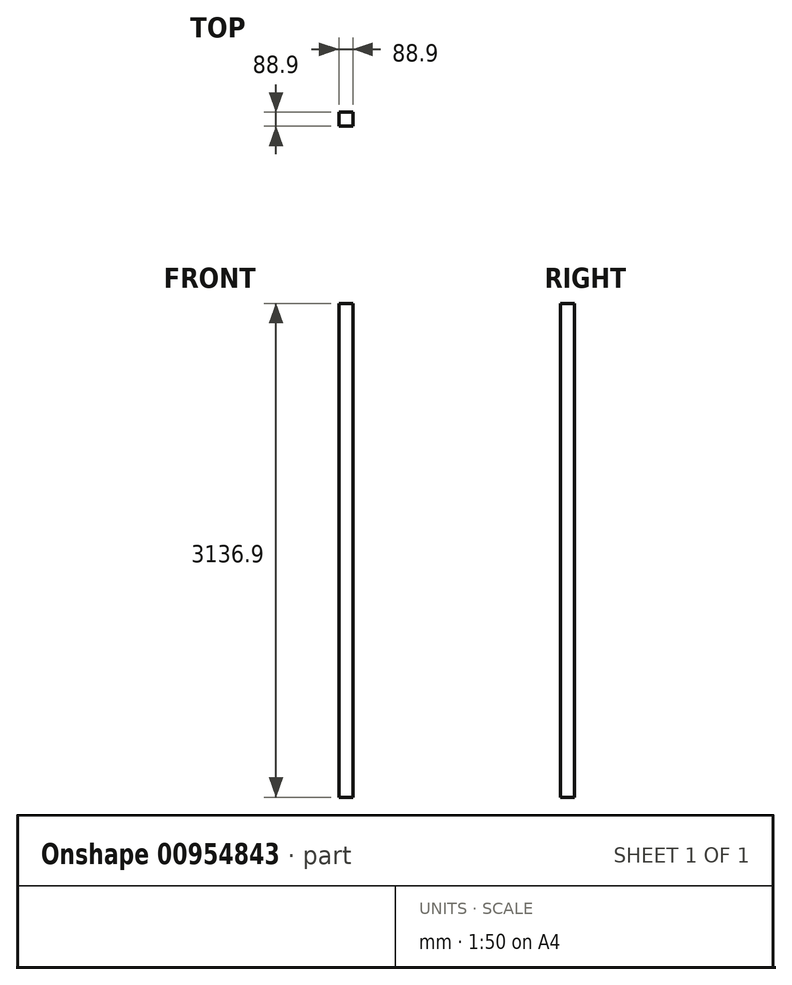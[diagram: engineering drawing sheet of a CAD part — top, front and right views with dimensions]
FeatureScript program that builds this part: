
annotation { "Feature Type Name" : "Feature", "Feature Type Description" : "" }
export const myFeature = defineFeature(function(context is Context, id is Id, definition is map)
    precondition{}
    {
        {
            var Q0;
            Q0=qCreatedBy(makeId("Top.planeOp"),FACE);
            var sketch = newSketch(context, id + "F0", { "sketchPlane" : qUnion([Q0])});
            skLineSegment(sketch, "E0.bottom", {"start": v(-44.45, 44.45) * mm, "end": v(44.45, 44.45) * mm});
            skLineSegment(sketch, "E0.top", {"start": v(-44.45, -44.45) * mm, "end": v(44.45, -44.45) * mm});
            skLineSegment(sketch, "E0.left", {"start": v(-44.45, 44.45) * mm, "end": v(-44.45, -44.45) * mm});
            skLineSegment(sketch, "E0.right", {"start": v(44.45, 44.45) * mm, "end": v(44.45, -44.45) * mm});
            skPoint(sketch, "E1", {"position": v(-44.45, 0) * mm});
            skPoint(sketch, "E2", {"position": v(0, 44.45) * mm});
            skSolve(sketch);
        }
        {
            var Q0;
            Q0 = qSketchRegion(id + "F0", true);
            extrude(context, id + "F1", {"entities" : qUnion([Q0]), "depth" : 2527.3 * mm, "offsetDistance" : 25.4 * mm, "hasSecondDirection" : true, "secondDirectionOppositeDirection" : true, "secondDirectionDepth" : 609.6 * mm});
        }
    });
